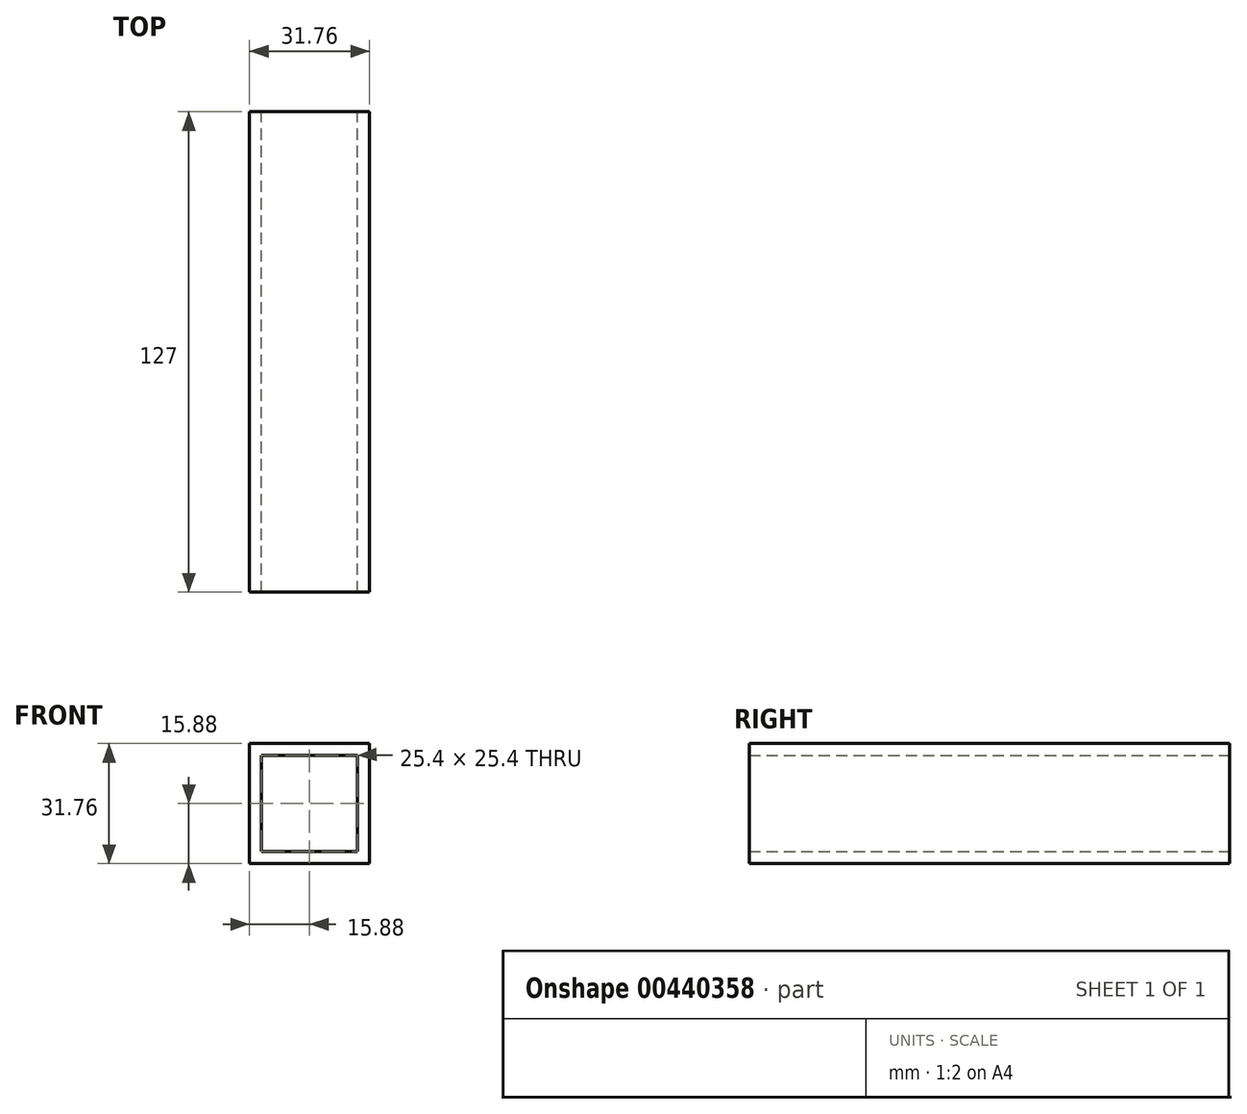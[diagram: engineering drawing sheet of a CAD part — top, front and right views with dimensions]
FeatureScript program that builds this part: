
annotation { "Feature Type Name" : "Feature", "Feature Type Description" : "" }
export const myFeature = defineFeature(function(context is Context, id is Id, definition is map)
    precondition{}
    {
        {
            var Q0;
            Q0=qCreatedBy(makeId("Front.planeOp"),FACE);
            var sketch = newSketch(context, id + "F0", { "sketchPlane" : qUnion([Q0])});
            skLineSegment(sketch, "E0.bottom", {"start": v(-15.87, 15.88) * mm, "end": v(15.88, 15.88) * mm});
            skLineSegment(sketch, "E0.top", {"start": v(-15.88, -15.88) * mm, "end": v(15.87, -15.88) * mm});
            skLineSegment(sketch, "E0.left", {"start": v(-15.87, 15.88) * mm, "end": v(-15.88, -15.88) * mm});
            skLineSegment(sketch, "E0.right", {"start": v(15.88, 15.88) * mm, "end": v(15.87, -15.88) * mm});
            skPoint(sketch, "E0.middle", {"position": v(0, 0) * mm});
            skLineSegment(sketch, "E1.bottom", {"start": v(-12.7, 12.7) * mm, "end": v(12.7, 12.7) * mm});
            skLineSegment(sketch, "E1.top", {"start": v(-12.7, -12.7) * mm, "end": v(12.7, -12.7) * mm});
            skLineSegment(sketch, "E1.left", {"start": v(-12.7, 12.7) * mm, "end": v(-12.7, -12.7) * mm});
            skLineSegment(sketch, "E1.right", {"start": v(12.7, 12.7) * mm, "end": v(12.7, -12.7) * mm});
            skSolve(sketch);
        }
        {
            var Q0;
            Q0=makeQuery(id+"F0.imprint","IMPRINT",FACE,{"disambiguationData":[TD([[makeQuery(id+"F0.imprint","IMPRINT",EDGE,{"derivedFrom":sQuery(id+"F0.wireOp",EDGE,"E0.bottom")}),-1.0]])]});
            extrude(context, id + "F1", {"entities" : qUnion([Q0]), "endBound" : BoundingType.SYMMETRIC, "depth" : 127 * mm});
        }
    });
